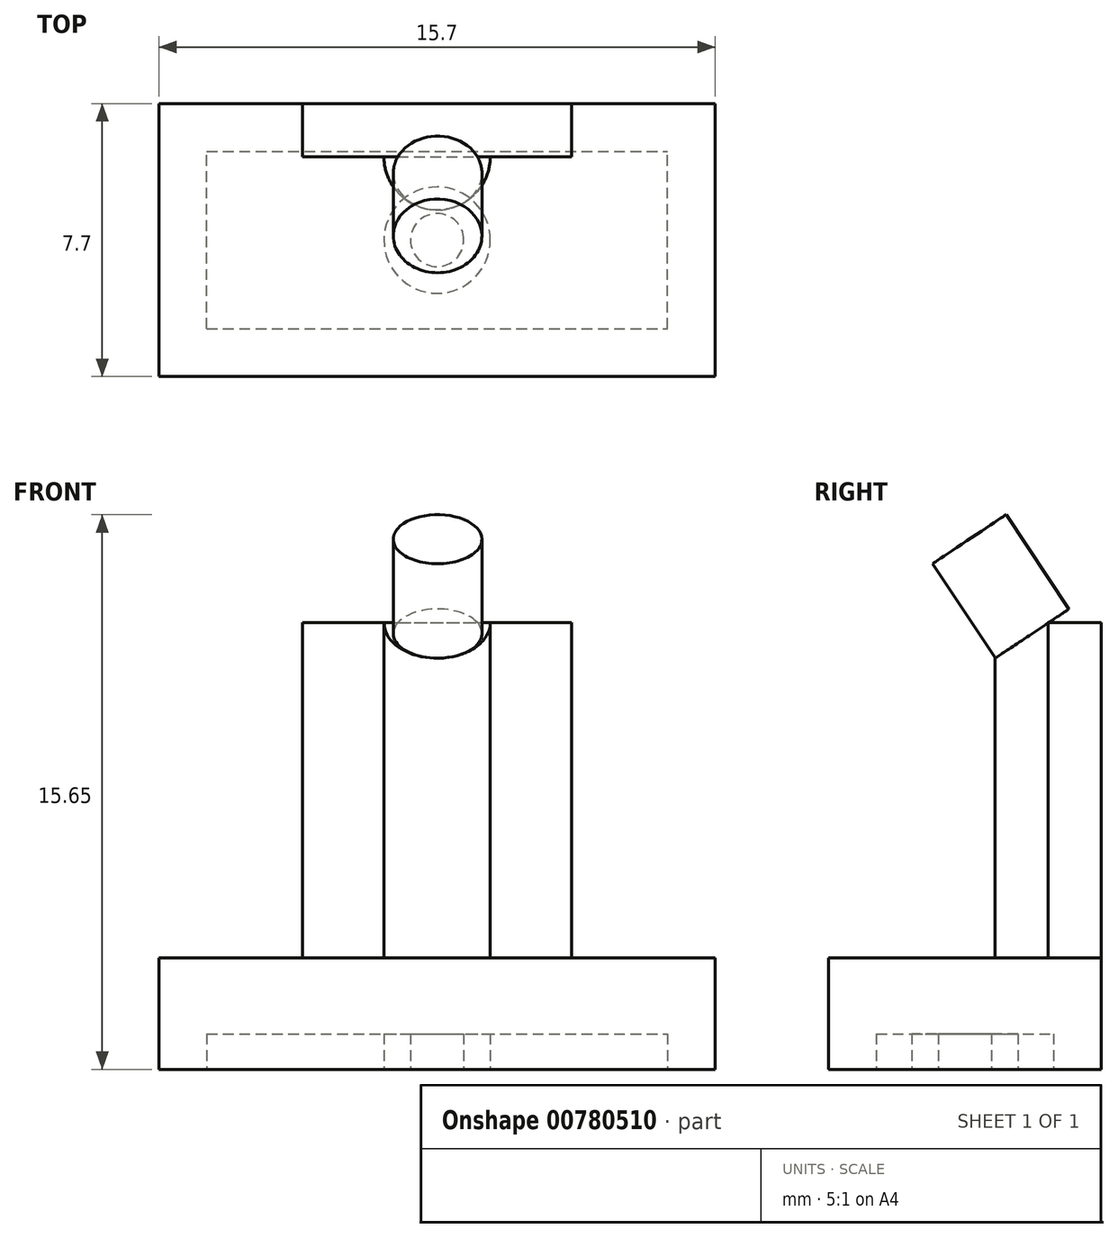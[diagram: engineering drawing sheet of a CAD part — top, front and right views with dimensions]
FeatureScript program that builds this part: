
annotation { "Feature Type Name" : "Feature", "Feature Type Description" : "" }
export const myFeature = defineFeature(function(context is Context, id is Id, definition is map)
    precondition{}
    {
        {
            var Q0;
            Q0=qCreatedBy(makeId("Front.planeOp"),FACE);
            var sketch = newSketch(context, id + "F0", { "sketchPlane" : qUnion([Q0])});
            skLineSegment(sketch, "E0.bottom", {"start": v(0, 0) * mm, "end": v(15.7, 0) * mm});
            skLineSegment(sketch, "E0.top", {"start": v(0, 3.15) * mm, "end": v(15.7, 3.15) * mm});
            skLineSegment(sketch, "E0.left", {"start": v(0, 0) * mm, "end": v(0, 3.15) * mm});
            skLineSegment(sketch, "E0.right", {"start": v(15.7, 0) * mm, "end": v(15.7, 3.15) * mm});
            skLineSegment(sketch, "E1", {"start": v(4.05, 3.15) * mm, "end": v(4.05, 12.6) * mm});
            skLineSegment(sketch, "E2", {"start": v(4.05, 12.6) * mm, "end": v(11.65, 12.6) * mm});
            skLineSegment(sketch, "E3", {"start": v(11.65, 12.6) * mm, "end": v(11.65, 3.15) * mm});
            skSolve(sketch);
        }
        {
            var Q0;
            Q0=makeQuery(id+"F0.imprint","IMPRINT",FACE,{"disambiguationData":[TD([[makeQuery(id+"F0.imprint","IMPRINT",EDGE,{"derivedFrom":sQuery(id+"F0.wireOp",EDGE,"E0.bottom")}),1.0]])]});
            extrude(context, id + "F1", {"entities" : qUnion([Q0]), "depth" : 7.7 * mm, "offsetDistance" : 25 * mm});
        }
        {
            var Q0;
            {var subQ0=sQuery(id+"F0.wireOp",EDGE,"E1");Q0=makeQuery(id+"F0.imprint","IMPRINT",FACE,{"disambiguationData":[TD([[makeQuery(id+"F0.imprint","IMPRINT",EDGE,{"derivedFrom":subQ0}),-1.0]])]});}
            extrude(context, id + "F2", {"entities" : qUnion([Q0]), "operationType" : NewBodyOperationType.ADD, "depth" : 1.5 * mm, "offsetDistance" : 25 * mm});
        }
        {
            var Q0;
            Q0=makeQuery(id+"F1.opExtrude","SWEPT_FACE",FACE,{"disambiguationData":[OSD([sQuery(id+"F0.wireOp",EDGE,"E0.top")])]});
            var sketch = newSketch(context, id + "F3", { "sketchPlane" : qUnion([Q0])});
            skCircle(sketch, "E4", {"center": v(7.85, -1.5) * mm, "radius": 1.5 * mm});
            skSolve(sketch);
        }
        {
            var Q0;
            Q0 = qSketchRegion(id + "F3", true);
            extrude(context, id + "F4", {"entities" : qUnion([Q0]), "operationType" : NewBodyOperationType.ADD, "depth" : 9.45 * mm, "offsetDistance" : 25 * mm});
        }
        {
            var Q0;
            Q0=makeQuery(id+"F1.opExtrude","SWEPT_FACE",FACE,{"disambiguationData":[OSD([sQuery(id+"F0.wireOp",EDGE,"E0.bottom")])]});
            var sketch = newSketch(context, id + "F5", { "sketchPlane" : qUnion([Q0])});
            skLineSegment(sketch, "E5.0", {"start": v(1.35, 6.35) * mm, "end": v(14.35, 6.35) * mm});
            skLineSegment(sketch, "E5.1", {"start": v(1.35, 6.35) * mm, "end": v(1.35, 1.35) * mm});
            skLineSegment(sketch, "E5.2", {"start": v(1.35, 1.35) * mm, "end": v(14.35, 1.35) * mm});
            skLineSegment(sketch, "E5.3", {"start": v(14.35, 6.35) * mm, "end": v(14.35, 1.35) * mm});
            skCircle(sketch, "E6", {"center": v(7.85, 3.85) * mm, "radius": 1.5 * mm});
            skPoint(sketch, "E6.centerSnap0", {"position": v(1.35, 3.85) * mm});
            skPoint(sketch, "E6.centerSnap1", {"position": v(7.85, 6.35) * mm});
            skCircle(sketch, "E7", {"center": v(7.85, 3.85) * mm, "radius": 0.75 * mm});
            skSolve(sketch);
        }
        {
            var Q0;
            Q0=makeQuery(id+"F5.imprint","IMPRINT",FACE,{"disambiguationData":[TD([[makeQuery(id+"F5.imprint","IMPRINT",EDGE,{"derivedFrom":sQuery(id+"F5.wireOp",EDGE,"E5.0")}),-1.0]])]});
            var Q1;
            Q1=makeQuery(id+"F5.imprint","IMPRINT",FACE,{"disambiguationData":[TD([[makeQuery(id+"F5.imprint","IMPRINT",EDGE,{"derivedFrom":sQuery(id+"F5.wireOp",EDGE,"E7")}),1.0]])]});
            extrude(context, id + "F6", {"entities" : qUnion([Q0, Q1]), "operationType" : NewBodyOperationType.REMOVE, "oppositeDirection" : true, "depth" : 1 * mm, "offsetDistance" : 25 * mm});
        }
        {
            var Q0;
            Q0=makeQuery(id+"F2.opExtrude","SWEPT_FACE",FACE,{"disambiguationData":[OSD([sQuery(id+"F0.wireOp",EDGE,"E3")])]});
            var sketch = newSketch(context, id + "F7", { "sketchPlane" : qUnion([Q0])});
            skLineSegment(sketch, "E8", {"start": v(-1.5, 12.6) * mm, "end": v(-3, 12.6) * mm});
            skLineSegment(sketch, "E9", {"start": v(-3, 12.6) * mm, "end": v(-3, 11.6) * mm});
            skLineSegment(sketch, "E10", {"start": v(-3, 11.6) * mm, "end": v(-1.5, 12.6) * mm});
            skSolve(sketch);
        }
        {
            var Q0;
            Q0 = qSketchRegion(id + "F7", true);
            extrude(context, id + "F8", {"entities" : qUnion([Q0]), "operationType" : NewBodyOperationType.REMOVE, "oppositeDirection" : true, "depth" : 25 * mm, "offsetDistance" : 25 * mm});
        }
        {
            var Q0;
            Q0=makeQuery(id+"F8.boolean.opBoolean","COPY",FACE,{"derivedFrom":makeQuery(id+"F8.opExtrude","SWEPT_FACE",FACE,{"disambiguationData":[OSD([sQuery(id+"F7.wireOp",EDGE,"E10")])]})});
            var sketch = newSketch(context, id + "F9", { "sketchPlane" : qUnion([Q0])});
            skCircle(sketch, "E11", {"center": v(7.86, 5.2) * mm, "radius": 1.25 * mm});
            skSolve(sketch);
        }
        {
            var Q0;
            Q0 = qSketchRegion(id + "F9", true);
            extrude(context, id + "F10", {"entities" : qUnion([Q0]), "operationType" : NewBodyOperationType.ADD, "depth" : 3.2 * mm, "offsetDistance" : 25 * mm});
        }
    });
